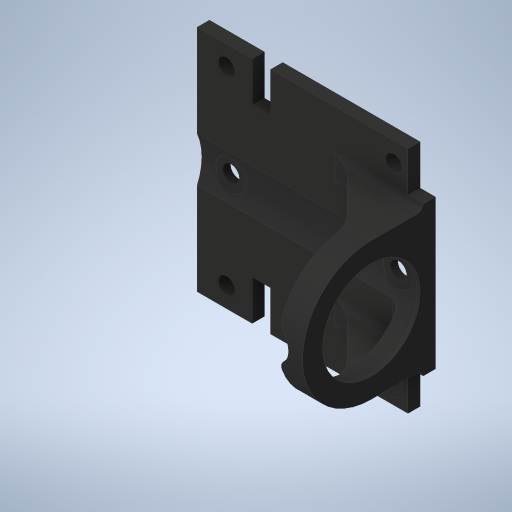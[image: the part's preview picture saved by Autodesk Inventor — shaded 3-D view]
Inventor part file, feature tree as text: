
AUTODESK INVENTOR PART (.ipt)
format: ipt  version: 2024 (Build 280153000, 153)  size: 847,360 bytes
history: native  units: mm
features: extrude x38, sketch x38, chamfer x6, pattern_linear x5, fillet x5, other x4, mirror x2
ambient origin geometry x8: Origin, YZ Plane, XZ Plane, XY Plane, X Axis, Y Axis, Z Axis, Center Point
bodies: Body1 (feature_tree)
feature tree (98):
  other  "Bryła1"
  extrude  "Wyciągnięcie proste1"  Depth=74.0mm
  extrude  "Wyciągnięcie proste2"  Depth=74.0mm
  extrude  "Wyciągnięcie proste3"  Depth=25.0mm TaperAngle=0.0deg
  extrude  "Wyciągnięcie proste4"  Depth=20.0mm
  other  "Płaszczyzna konstrukcyjna1"
  extrude  "Wyciągnięcie proste5"  Depth=20.0mm
  pattern_linear  "Szyk prostokątny1"  Spacing1=11.0mm  [1 undecoded]
  chamfer  "Faza1"  Distance=11.0mm
  chamfer  "Faza2"  Distance=19.8mm
  chamfer  "Faza3"  Distance=2.05mm
  extrude  "Wyciągnięcie proste6"  Depth=7.9mm
  extrude  "Wyciągnięcie proste7"  TaperAngle=0.0deg  [1 undecoded]
  extrude  "Wyciągnięcie proste8"  TaperAngle=0.0deg  [1 undecoded]
  extrude  "Wyciągnięcie proste9"  Depth=2.05mm
  extrude  "Wyciągnięcie proste10"  Depth=7.9mm
  extrude  "Wyciągnięcie proste11"  TaperAngle=0.0deg  [1 undecoded]
  pattern_linear  "Szyk prostokątny2"  Spacing1=0.0mm  [1 undecoded]
  extrude  "Wyciągnięcie proste12"  Depth=1.9mm TaperAngle=0.0deg
  other  "Płaszczyzna konstrukcyjna2"
  mirror  "Odbij1"
  chamfer  "Faza4"  Distance=4.0mm
  extrude  "Wyciągnięcie proste13"  Depth=5.5mm
  pattern_linear  "Szyk prostokątny3"  Spacing1=5.5mm  [1 undecoded]
  extrude  "Wyciągnięcie proste14"  Depth=6.0mm
  pattern_linear  "Szyk prostokątny4"  Spacing1=6.0mm  [1 undecoded]
  extrude  "Wyciągnięcie proste15"  Depth=54.78mm
  pattern_linear  "Szyk prostokątny5"  Spacing1=-37.0mm  [1 undecoded]
  extrude  "Wyciągnięcie proste16"  Depth=27.39mm
  other  "Płaszczyzna konstrukcyjna3"
  mirror  "Odbij2"
  extrude  "Wyciągnięcie proste17"  Depth=50.0mm TaperAngle=0.0deg
  extrude  "Wyciągnięcie proste18"  Depth=30.0mm
  extrude  "Wyciągnięcie proste19"  Depth=2.0mm TaperAngle=45.0deg
  extrude  "Wyciągnięcie proste20"  Depth=2.0mm TaperAngle=45.0deg
  extrude  "Wyciągnięcie proste21"  Depth=2.0mm TaperAngle=45.0deg
  chamfer  "Faza5"  Distance=22.9mm
  extrude  "Wyciągnięcie proste23"  Depth=12.0mm
  extrude  "Wyciągnięcie proste25"  Depth=12.0mm
  extrude  "Wyciągnięcie proste26"  Depth=100.0mm
  extrude  "Wyciągnięcie proste24"  Depth=13.0mm
  extrude  "Wyciągnięcie proste27"  Depth=13.0mm
  chamfer  "Faza6"  Distance=25.0mm
  fillet  "Zaokrąglenie1"  Radius=25.0mm
  extrude  "Wyciągnięcie proste28"  Depth=25.0mm
  fillet  "Zaokrąglenie2"  Radius=55.0mm
  extrude  "Wyciągnięcie proste29"  TaperAngle=0.0deg  [1 undecoded]
  extrude  "Wyciągnięcie proste30"  Depth=0.5mm
  extrude  "Wyciągnięcie proste32"  Depth=0.5mm
  extrude  "Wyciągnięcie proste33"  Depth=74.0mm TaperAngle=0.0deg
  extrude  "Wyciągnięcie proste34"  Depth=55.0mm TaperAngle=0.0deg
  extrude  "Wyciągnięcie proste37"  Depth=55.0mm TaperAngle=0.0deg
  extrude  "Wyciągnięcie proste38"  Depth=3.5mm
  extrude  "Wyciągnięcie proste39"  Depth=13.1mm
  fillet  "Zaokrąglenie3"  Radius=13.0mm
  extrude  "Wyciągnięcie proste40"  Depth=5000.0mm TaperAngle=0.0deg
  extrude  "Wyciągnięcie proste41"  Depth=30.0mm
  extrude  "Wyciągnięcie proste42"  Depth=11.0mm
  fillet  "Zaokrąglenie4"  Radius=11.0mm
  fillet  "Zaokrąglenie5"  Radius=5.0mm
  sketch  "Szkic1"
  sketch  "Szkic2"
  sketch  "Szkic3"
  sketch  "Szkic4"
  sketch  "Szkic5"
  sketch  "Szkic6"
  sketch  "Szkic7"
  sketch  "Szkic8"
  sketch  "Szkic9"
  sketch  "Szkic10"
  sketch  "Szkic12"
  sketch  "Szkic13"
  sketch  "Szkic15"
  sketch  "Szkic16"
  sketch  "Szkic17"
  sketch  "Szkic18"
  sketch  "Szkic19"
  sketch  "Szkic20"
  sketch  "Szkic21"
  sketch  "Szkic22"
  sketch  "Szkic23"
  sketch  "Szkic25"
  sketch  "Szkic26"
  sketch  "Szkic27"
  sketch  "Szkic29"
  sketch  "Szkic30"
  sketch  "Szkic31"
  sketch  "Szkic33"
  sketch  "Szkic34"
  sketch  "Szkic35"
  sketch  "Szkic36"
  sketch  "Szkic37"
  sketch  "Szkic41"
  sketch  "Szkic42"
  sketch  "Szkic43"
  sketch  "Szkic44"
  sketch  "Szkic46"
  sketch  "Szkic47"
note: 9 required parameter values undecoded (feature->parameter linkage not recoverable at this tier; creation-order binding heuristic only, values carry confidence <= 0.55)
